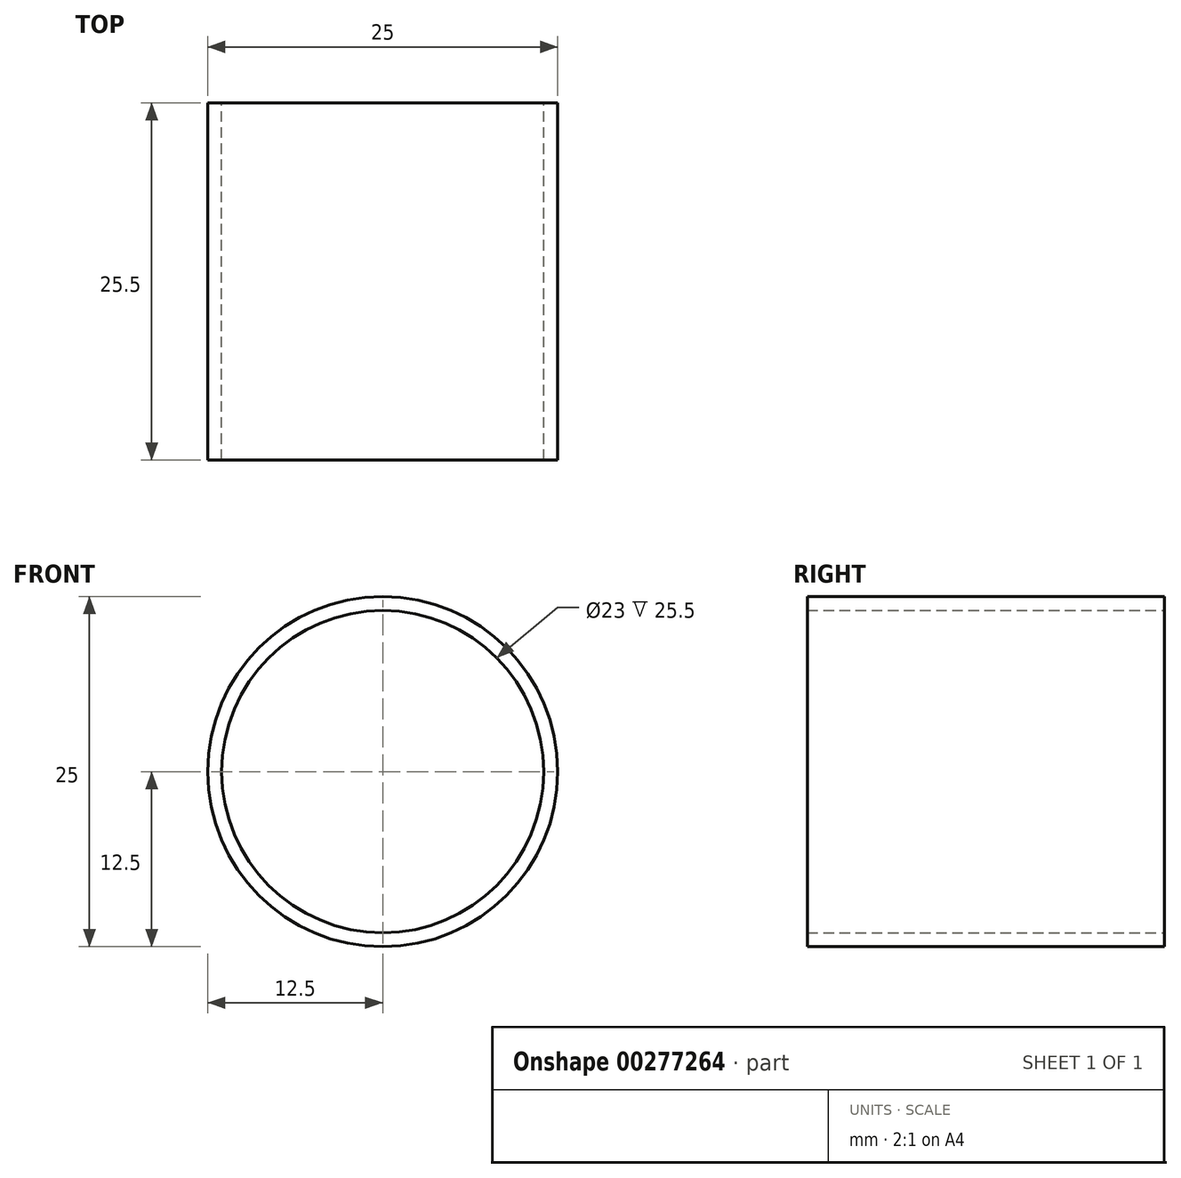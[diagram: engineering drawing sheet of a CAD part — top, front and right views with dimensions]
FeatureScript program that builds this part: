
annotation { "Feature Type Name" : "Feature", "Feature Type Description" : "" }
export const myFeature = defineFeature(function(context is Context, id is Id, definition is map)
    precondition{}
    {
        {
            var Q0;
            Q0=qCreatedBy(makeId("Front.planeOp"),FACE);
            var sketch = newSketch(context, id + "F0", { "sketchPlane" : qUnion([Q0])});
            skCircle(sketch, "E0", {"center": v(0, 0) * mm, "radius": 12.5 * mm});
            skCircle(sketch, "E1", {"center": v(0, 0) * mm, "radius": 11.5 * mm});
            skSolve(sketch);
        }
        {
            var Q0;
            Q0=makeQuery(id+"F0.imprint","IMPRINT",FACE,{"disambiguationData":[TD([[makeQuery(id+"F0.imprint","IMPRINT",EDGE,{"derivedFrom":sQuery(id+"F0.wireOp",EDGE,"E0")}),1.0]])]});
            extrude(context, id + "F1", {"entities" : qUnion([Q0]), "depth" : 25.5 * mm});
        }
    });
